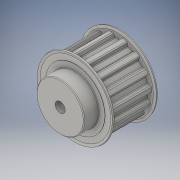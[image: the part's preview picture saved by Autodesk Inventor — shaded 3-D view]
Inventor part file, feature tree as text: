
AUTODESK INVENTOR PART (.ipt)
format: ipt  version: 2016 (Build 200138000, 138)  size: 367,104 bytes
history: native  units: in
note: dims shown in document units (in); Inventor stores cm internally (conversion verified against a paired STEP export)
features: other x3, sketch x1
ambient origin geometry x8: Origin, YZ Plane, XZ Plane, XY Plane, X Axis, Y Axis, Z Axis, Center Point
bodies: Solid1 (feature_tree)
feature tree (4):
  other  "ls40t10_15-2_hub-32x10_d-8h7.ipt"
  other  "Solid1::ls40t10_15-2_hub-32x10_d-8h7.ipt"
  other  "TaggingFeature1"
  sketch  "Sketch1"  dims[d0=0.3937in]
